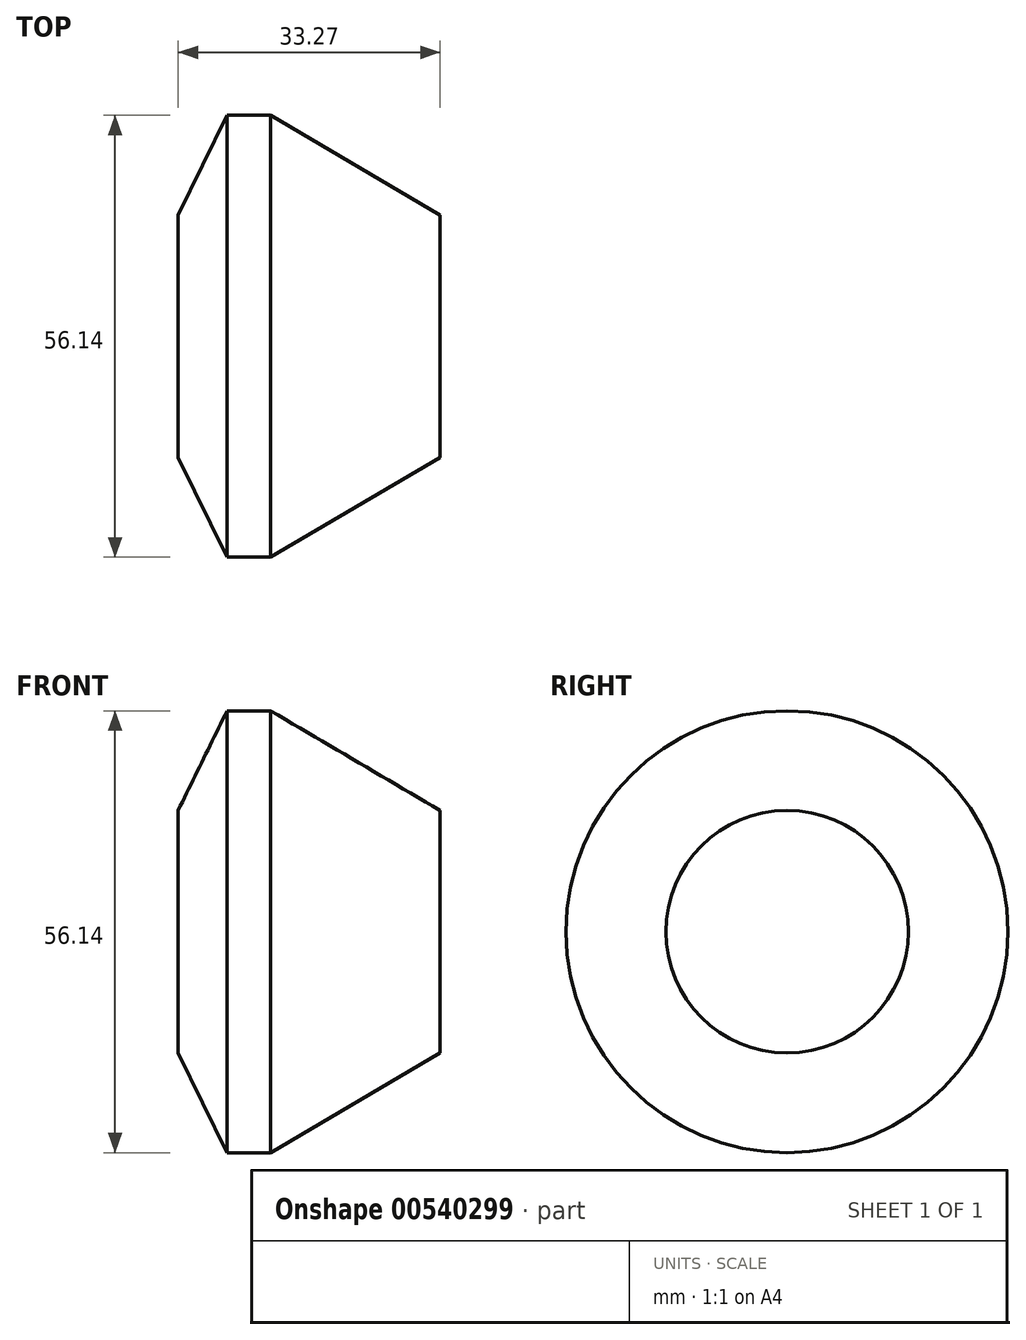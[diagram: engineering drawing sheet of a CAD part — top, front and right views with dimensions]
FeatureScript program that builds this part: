
annotation { "Feature Type Name" : "Feature", "Feature Type Description" : "" }
export const myFeature = defineFeature(function(context is Context, id is Id, definition is map)
    precondition{}
    {
        {
            var Q0;
            Q0=qCreatedBy(makeId("Front.planeOp"),FACE);
            var sketch = newSketch(context, id + "F0", { "sketchPlane" : qUnion([Q0])});
            skLineSegment(sketch, "E0", {"start": v(0, 0) * mm, "end": v(23.7, 0) * mm});
            skLineSegment(sketch, "E1", {"start": v(23.7, 0) * mm, "end": v(23.7, 15.4) * mm});
            skLineSegment(sketch, "E2", {"start": v(23.7, 15.4) * mm, "end": v(2.17, 28.07) * mm});
            skLineSegment(sketch, "E3", {"start": v(2.17, 28.07) * mm, "end": v(-3.37, 28.07) * mm});
            skLineSegment(sketch, "E4", {"start": v(-3.37, 28.07) * mm, "end": v(-9.57, 15.4) * mm});
            skLineSegment(sketch, "E5", {"start": v(-9.57, 15.4) * mm, "end": v(-9.57, 0) * mm});
            skLineSegment(sketch, "E6", {"start": v(-9.57, 0) * mm, "end": v(0, 0) * mm});
            skSolve(sketch);
        }
        {
            var Q0;
            Q0=makeQuery(id+"F0.imprint","IMPRINT",FACE,{"disambiguationData":[TD([[makeQuery(id+"F0.imprint","IMPRINT",EDGE,{"derivedFrom":sQuery(id+"F0.wireOp",EDGE,"E0")}),1.0]])]});
            var Q1;
            Q1=sQuery(id+"F0.wireOp",EDGE,"E0");
            revolve(context, id + "F1", {"entities" : qUnion([Q0]), "axis" : qUnion([Q1]), "revolveType" : RevolveType.FULL});
        }
    });
